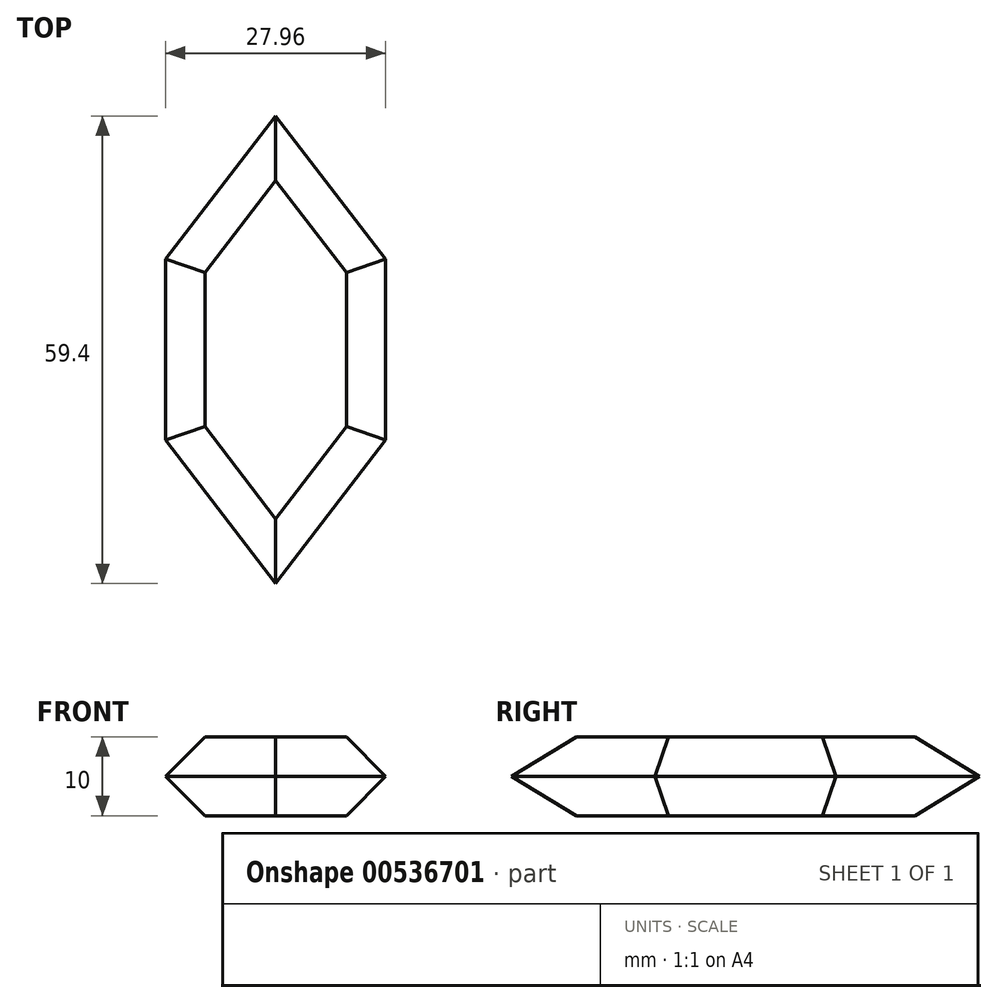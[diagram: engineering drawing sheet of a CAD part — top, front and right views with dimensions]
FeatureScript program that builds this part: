
annotation { "Feature Type Name" : "Feature", "Feature Type Description" : "" }
export const myFeature = defineFeature(function(context is Context, id is Id, definition is map)
    precondition{}
    {
        {
            var Q0;
            Q0=qCreatedBy(makeId("Top.planeOp"),FACE);
            var sketch = newSketch(context, id + "F0", { "sketchPlane" : qUnion([Q0])});
            skLineSegment(sketch, "E0", {"start": v(-13.98, 11.48) * mm, "end": v(-13.98, -11.48) * mm});
            skLineSegment(sketch, "E1", {"start": v(-13.98, -11.48) * mm, "end": v(0, -29.7) * mm});
            skLineSegment(sketch, "E2", {"start": v(0, -29.7) * mm, "end": v(13.98, -11.48) * mm});
            skLineSegment(sketch, "E3", {"start": v(13.98, -11.48) * mm, "end": v(13.98, 11.48) * mm});
            skLineSegment(sketch, "E4", {"start": v(13.98, 11.48) * mm, "end": v(0, 29.7) * mm});
            skLineSegment(sketch, "E5", {"start": v(0, 29.7) * mm, "end": v(-13.98, 11.48) * mm});
            skSolve(sketch);
        }
        {
            var Q0;
            Q0=makeQuery(id+"F0.imprint","IMPRINT",FACE,{"disambiguationData":[TD([[makeQuery(id+"F0.imprint","IMPRINT",EDGE,{"derivedFrom":sQuery(id+"F0.wireOp",EDGE,"E0")}),1.0]])]});
            extrude(context, id + "F1", {"entities" : qUnion([Q0]), "depth" : 5 * mm, "offsetDistance" : 25 * mm, "hasDraft" : true, "draftAngle" : 45 * degree, "draftPullDirection" : true});
        }
        {
            var Q0;
            Q0=makeQuery(id+"F1.opExtrude","SWEPT_BODY",BODY,{"disambiguationData":[OSD([sQuery(id+"F0.wireOp",EDGE,"E0"),sQuery(id+"F0.wireOp",EDGE,"E1"),sQuery(id+"F0.wireOp",EDGE,"E2"),sQuery(id+"F0.wireOp",EDGE,"E3"),sQuery(id+"F0.wireOp",EDGE,"E4"),sQuery(id+"F0.wireOp",EDGE,"E5")])]});
            var Q1;
            Q1=qCreatedBy(makeId("Top.planeOp"),FACE);
            mirror(context, id + "F2", {"operationType" : NewBodyOperationType.ADD, "entities" : qUnion([Q0]), "mirrorPlane" : qUnion([Q1])});
        }
    });
